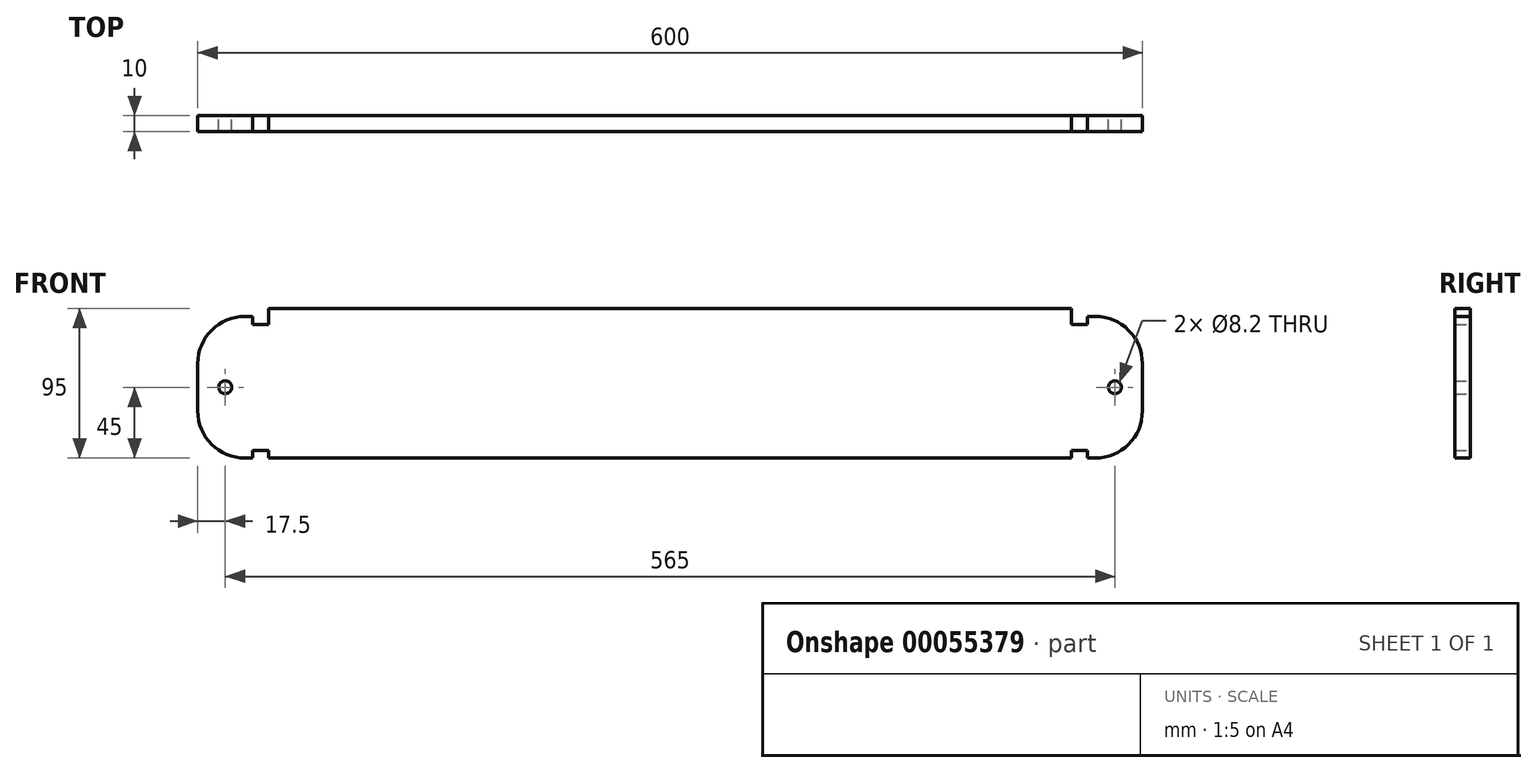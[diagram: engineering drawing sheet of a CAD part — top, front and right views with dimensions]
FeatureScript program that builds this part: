
annotation { "Feature Type Name" : "Feature", "Feature Type Description" : "" }
export const myFeature = defineFeature(function(context is Context, id is Id, definition is map)
    precondition{}
    {
        {
            var Q0;
            Q0=qCreatedBy(makeId("Top.planeOp"),FACE);
            var sketch = newSketch(context, id + "F0", { "sketchPlane" : qUnion([Q0])});
            skLineSegment(sketch, "E0.rect.bottom", {"start": v(-300, 45) * mm, "end": v(-265, 45) * mm});
            skLineSegment(sketch, "E0.rect.top", {"start": v(-300, -45) * mm, "end": v(-265, -45) * mm});
            skLineSegment(sketch, "E0.rect.left", {"start": v(-300, 45) * mm, "end": v(-300, -45) * mm});
            skLineSegment(sketch, "E0.rect.right", {"start": v(300, 45) * mm, "end": v(300, -45) * mm});
            skPoint(sketch, "E0.rect.middle", {"position": v(0, 0) * mm});
            skLineSegment(sketch, "E1", {"start": v(0, 45) * mm, "end": v(0, -111.76) * mm, "construction": true});
            skPoint(sketch, "E1.endSnap0", {"position": v(0, -45) * mm});
            skPoint(sketch, "E2.endSnap0", {"position": v(300, 0) * mm});
            skLineSegment(sketch, "E3.0", {"start": v(-265, -40) * mm, "end": v(-255, -40) * mm});
            skLineSegment(sketch, "E4.0", {"start": v(-265, 40) * mm, "end": v(-255, 40) * mm});
            skLineSegment(sketch, "E5.0", {"start": v(265, 45) * mm, "end": v(265, 40) * mm});
            skLineSegment(sketch, "E6.0", {"start": v(-265, 45) * mm, "end": v(-265, 40) * mm});
            skLineSegment(sketch, "E7.trimOffspring", {"start": v(255, 40) * mm, "end": v(265, 40) * mm});
            skLineSegment(sketch, "E8.trimOffspring", {"start": v(255, -40) * mm, "end": v(265, -40) * mm});
            skLineSegment(sketch, "E9.trimOffspring", {"start": v(-265, -40) * mm, "end": v(-265, -45) * mm});
            skLineSegment(sketch, "E10.trimOffspring", {"start": v(-255, -40) * mm, "end": v(-255, -45) * mm});
            skLineSegment(sketch, "E11.trimOffspring", {"start": v(265, -45) * mm, "end": v(300, -45) * mm});
            skLineSegment(sketch, "E12.trimOffspring", {"start": v(265, 45) * mm, "end": v(300, 45) * mm});
            skLineSegment(sketch, "E13.trimOffspring", {"start": v(265, -40) * mm, "end": v(265, -45) * mm});
            skLineSegment(sketch, "E14.trimOffspring", {"start": v(255, -40) * mm, "end": v(255, -45) * mm});
            skPoint(sketch, "E15", {"position": v(-282.5, 0) * mm});
            skPoint(sketch, "E16", {"position": v(282.5, 0) * mm});
            skCircle(sketch, "E17", {"center": v(-282.5, 0) * mm, "radius": 4.1 * mm});
            skCircle(sketch, "E18", {"center": v(282.5, 0) * mm, "radius": 4.1 * mm});
            skLineSegment(sketch, "E19", {"start": v(-255, -45) * mm, "end": v(255, -45) * mm});
            skLineSegment(sketch, "E20", {"start": v(-300, 0) * mm, "end": v(325.96, 0) * mm, "construction": true});
            skLineSegment(sketch, "E21.MirrorCS", {"start": v(-255, 50) * mm, "end": v(255, 50) * mm});
            skLineSegment(sketch, "E22", {"start": v(255, 40) * mm, "end": v(255, 50) * mm});
            skLineSegment(sketch, "E23", {"start": v(-255, 40) * mm, "end": v(-255, 50) * mm});
            skSolve(sketch);
        }
        {
            var Q0;
            Q0=makeQuery(id+"F0.imprint","IMPRINT",FACE,{"disambiguationData":[TD([[makeQuery(id+"F0.imprint","IMPRINT",EDGE,{"derivedFrom":sQuery(id+"F0.wireOp",EDGE,"E0.rect.bottom")}),-1.0]])]});
            extrude(context, id + "F1", {"entities" : qUnion([Q0]), "depth" : 10 * mm});
        }
        {
            var Q0;
            Q0=makeQuery(id+"F1.opExtrude","SWEPT_EDGE",EDGE,{"disambiguationData":[OSD([sQuery(id+"F0.wireOp",EDGE,"E0.rect.top"),sQuery(id+"F0.wireOp",EDGE,"E0.rect.left")])]});
            var Q1;
            Q1=makeQuery(id+"F1.opExtrude","SWEPT_EDGE",EDGE,{"disambiguationData":[OSD([sQuery(id+"F0.wireOp",EDGE,"E0.rect.bottom"),sQuery(id+"F0.wireOp",EDGE,"E0.rect.left")])]});
            var Q2;
            Q2=makeQuery(id+"F1.opExtrude","SWEPT_EDGE",EDGE,{"disambiguationData":[OSD([sQuery(id+"F0.wireOp",EDGE,"E0.rect.right"),sQuery(id+"F0.wireOp",EDGE,"E12.trimOffspring")])]});
            var Q3;
            Q3=makeQuery(id+"F1.opExtrude","SWEPT_EDGE",EDGE,{"disambiguationData":[OSD([sQuery(id+"F0.wireOp",EDGE,"E0.rect.right"),sQuery(id+"F0.wireOp",EDGE,"E11.trimOffspring")])]});
            fillet(context, id + "F2", {"entities" : qUnion([Q0, Q1, Q2, Q3]), "radius" : 30 * mm, "tangentPropagation" : true, "allowEdgeOverflow" : false});
        }
        {
            var Q0;
            Q0=makeQuery(id+"F1.opExtrude","SWEPT_BODY",BODY,{"disambiguationData":[OSD([sQuery(id+"F0.wireOp",EDGE,"E0.rect.bottom"),sQuery(id+"F0.wireOp",EDGE,"E0.rect.top"),sQuery(id+"F0.wireOp",EDGE,"E0.rect.left"),sQuery(id+"F0.wireOp",EDGE,"E0.rect.right"),sQuery(id+"F0.wireOp",EDGE,"E3.0"),sQuery(id+"F0.wireOp",EDGE,"E4.0"),sQuery(id+"F0.wireOp",EDGE,"90063e62-f2fd-471f-b875-fc58e48d3a71.0"),sQuery(id+"F0.wireOp",EDGE,"654737f6-0989-4e1a-8ec4-07799c683a42.0"),sQuery(id+"F0.wireOp",EDGE,"E5.0"),sQuery(id+"F0.wireOp",EDGE,"E6.0"),sQuery(id+"F0.wireOp",EDGE,"a43bbe40-a806-4a21-9d7e-a1d10adff70f.trimOffspring"),sQuery(id+"F0.wireOp",EDGE,"d7a5bf05-82e2-48a9-b6d0-5fe12b60c59c.trimOffspring"),sQuery(id+"F0.wireOp",EDGE,"E7.trimOffspring"),sQuery(id+"F0.wireOp",EDGE,"E8.trimOffspring"),sQuery(id+"F0.wireOp",EDGE,"E9.trimOffspring"),sQuery(id+"F0.wireOp",EDGE,"E10.trimOffspring"),sQuery(id+"F0.wireOp",EDGE,"E11.trimOffspring"),sQuery(id+"F0.wireOp",EDGE,"E12.trimOffspring"),sQuery(id+"F0.wireOp",EDGE,"E13.trimOffspring"),sQuery(id+"F0.wireOp",EDGE,"E14.trimOffspring"),sQuery(id+"F0.wireOp",EDGE,"E17"),sQuery(id+"F0.wireOp",EDGE,"E18")])]});
            var Q1;
            Q1=sQuery(id+"F0.wireOp",EDGE,"E11.trimOffspring");
            transform(context, id + "F3", {"entities" : qUnion([Q0]), "transformType" : TransformType.ROTATION, "transformAxis" : qUnion([Q1]), "angle" : 90 * degree, "makeCopy" : false});
        }
    });
